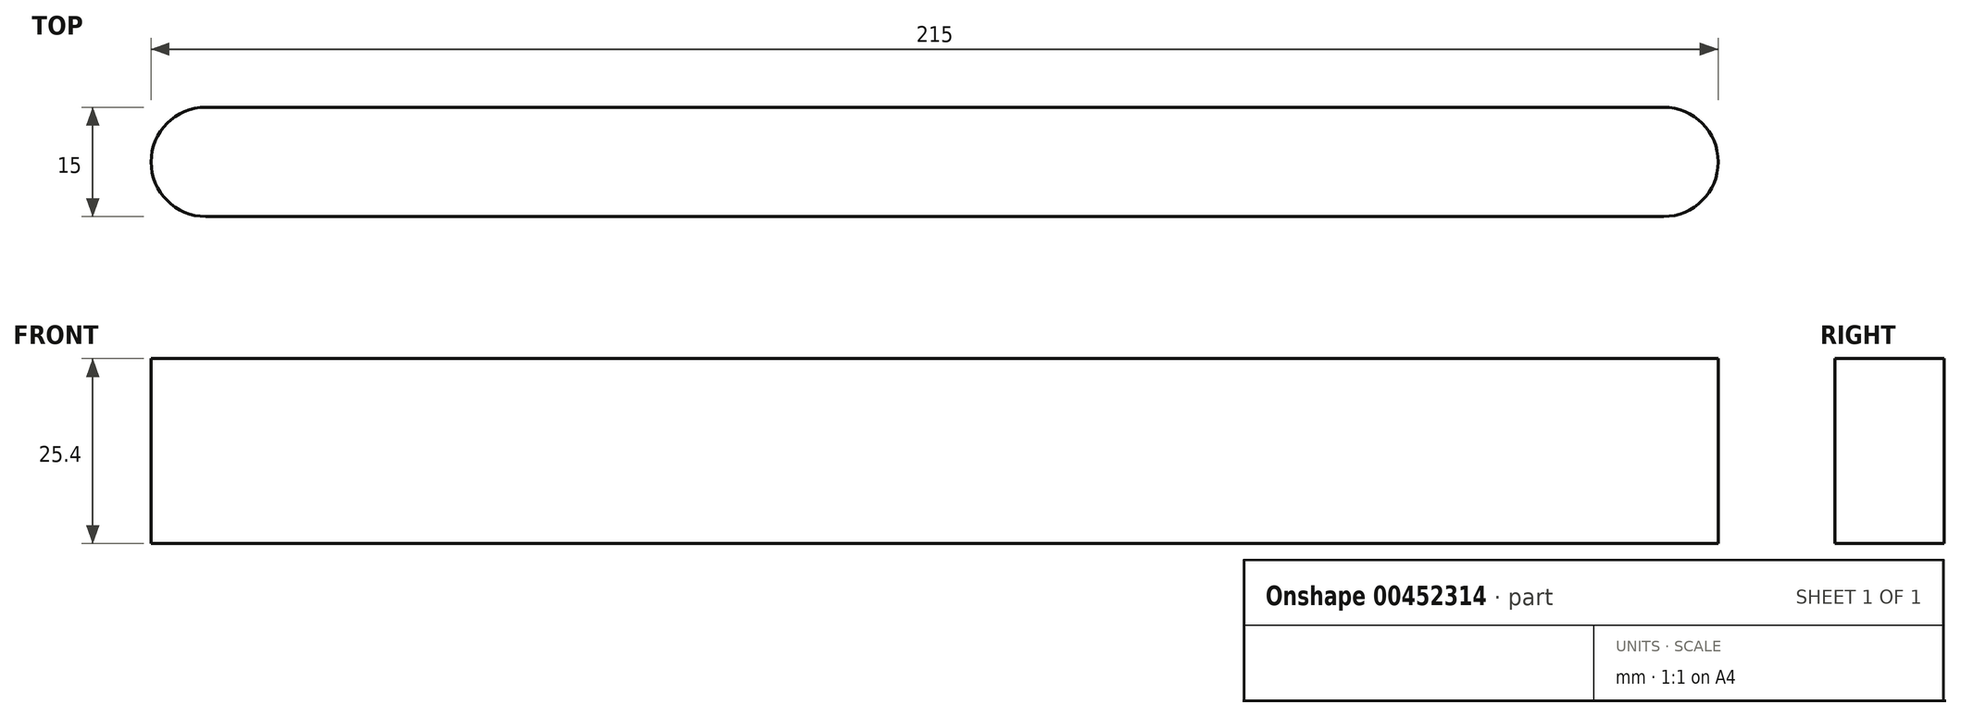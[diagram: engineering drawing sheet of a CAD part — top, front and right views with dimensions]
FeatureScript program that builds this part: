
annotation { "Feature Type Name" : "Feature", "Feature Type Description" : "" }
export const myFeature = defineFeature(function(context is Context, id is Id, definition is map)
    precondition{}
    {
        {
            var Q0;
            Q0=qCreatedBy(makeId("Top.planeOp"),FACE);
            var sketch = newSketch(context, id + "F0", { "sketchPlane" : qUnion([Q0])});
            skLineSegment(sketch, "E0.bottom", {"start": v(100, -7.5) * mm, "end": v(-100, -7.5) * mm});
            skLineSegment(sketch, "E0.top", {"start": v(100, 7.5) * mm, "end": v(-100, 7.5) * mm});
            skLineSegment(sketch, "E0.left", {"start": v(100, -7.5) * mm, "end": v(100, 7.5) * mm});
            skLineSegment(sketch, "E0.right", {"start": v(-100, -7.5) * mm, "end": v(-100, 7.5) * mm});
            skPoint(sketch, "E0.middle", {"position": v(0, 0) * mm});
            skCircle(sketch, "E1", {"center": v(-100, 0) * mm, "radius": 7.5 * mm});
            skCircle(sketch, "E2", {"center": v(100, 0) * mm, "radius": 7.5 * mm});
            skSolve(sketch);
        }
        {
            var Q0;
            Q0 = qSketchRegion(id + "F0", true);
            extrude(context, id + "F1", {"entities" : qUnion([Q0]), "depth" : 25.4 * mm});
        }
        {
            var Q0;
            Q0=makeQuery(id+"F1.opExtrude","CAP_FACE",FACE,{"disambiguationData":[OSD([sQuery(id+"F0.wireOp",EDGE,"E0.bottom"),sQuery(id+"F0.wireOp",EDGE,"E0.top"),sQuery(id+"F0.wireOp",EDGE,"E1"),sQuery(id+"F0.wireOp",EDGE,"E2")])],"isStart":false});
            var sketch = newSketch(context, id + "F2", { "sketchPlane" : qUnion([Q0])});
            skCircle(sketch, "E3", {"center": v(-107.5, 0) * mm, "radius": 1.14 * mm});
            skSolve(sketch);
        }
        {
            var Q0;
            {var subQ1=makeQuery(id+"F1.opExtrude","CAP_EDGE",EDGE,{"disambiguationData":[OSD([sQuery(id+"F0.wireOp",EDGE,"E0.bottom")])],"isStart":false});Q0=makeQuery(id+"F2.imprint","IMPRINT",FACE,{"disambiguationData":[TD([[makeQuery(id+"F2.imprint","IMPRINT",EDGE,{"derivedFrom":subQ1}),-1.0]])]});}
            var sketch = newSketch(context, id + "F3", { "sketchPlane" : qUnion([Q0])});
            skLineSegment(sketch, "E4", {"start": v(-107.47, 0) * mm, "end": v(-107.47, -108.18) * mm});
            skSolve(sketch);
        }
    });
